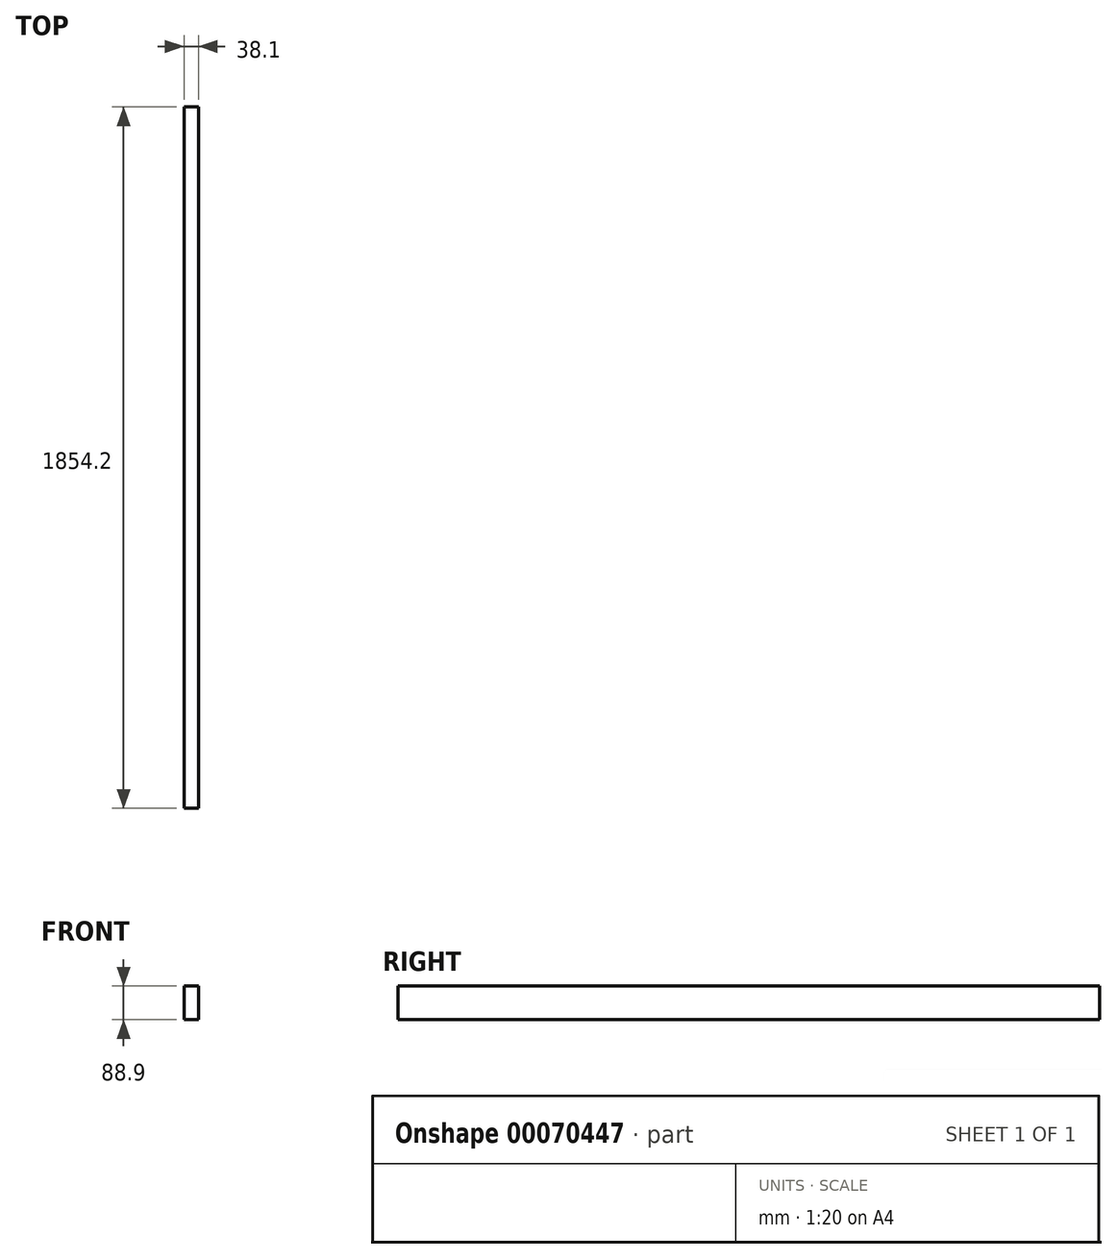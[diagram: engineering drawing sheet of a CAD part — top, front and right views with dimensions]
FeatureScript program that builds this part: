
annotation { "Feature Type Name" : "Feature", "Feature Type Description" : "" }
export const myFeature = defineFeature(function(context is Context, id is Id, definition is map)
    precondition{}
    {
        {
            var Q0;
            Q0=qCreatedBy(makeId("Front.planeOp"),FACE);
            var sketch = newSketch(context, id + "F0", { "sketchPlane" : qUnion([Q0])});
            skLineSegment(sketch, "E0.bottom", {"start": v(25.49, 8.78) * mm, "end": v(63.59, 8.78) * mm});
            skLineSegment(sketch, "E0.top", {"start": v(25.49, -80.12) * mm, "end": v(63.59, -80.12) * mm});
            skLineSegment(sketch, "E0.left", {"start": v(25.49, 8.78) * mm, "end": v(25.49, -80.12) * mm});
            skLineSegment(sketch, "E0.right", {"start": v(63.59, 8.78) * mm, "end": v(63.59, -80.12) * mm});
            skSolve(sketch);
        }
        {
            var Q0;
            Q0 = qSketchRegion(id + "F0", true);
            extrude(context, id + "F1", {"entities" : qUnion([Q0]), "oppositeDirection" : true, "depth" : 1854.2 * mm});
        }
    });
